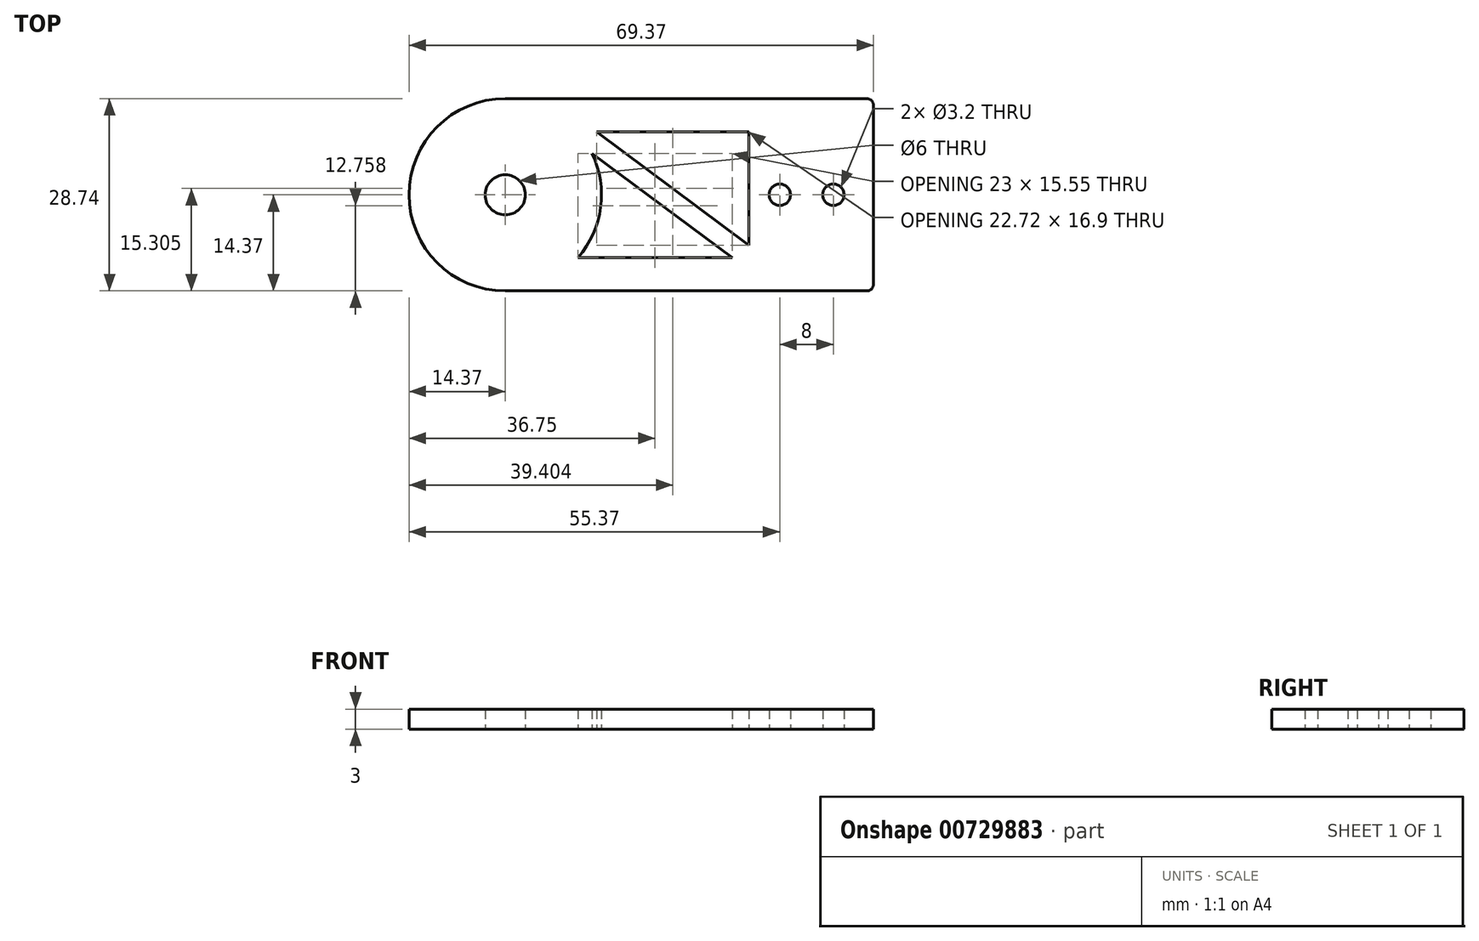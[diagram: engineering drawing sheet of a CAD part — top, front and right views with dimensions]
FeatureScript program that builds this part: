
annotation { "Feature Type Name" : "Feature", "Feature Type Description" : "" }
export const myFeature = defineFeature(function(context is Context, id is Id, definition is map)
    precondition{}
    {
        {
            var Q0;
            Q0=qCreatedBy(makeId("Top.planeOp"),FACE);
            var sketch = newSketch(context, id + "F0", { "sketchPlane" : qUnion([Q0])});
            skLineSegment(sketch, "E0.bottom", {"start": v(22.5, 0) * mm, "end": v(77.5, 0) * mm});
            skLineSegment(sketch, "E0.top", {"start": v(22.5, 28.74) * mm, "end": v(77.5, 28.74) * mm});
            skLineSegment(sketch, "E0.right", {"start": v(77.5, 0) * mm, "end": v(77.5, 28.74) * mm});
            skLineSegment(sketch, "E1", {"start": v(12.5, 14.37) * mm, "end": v(77.5, 14.37) * mm, "construction": true});
            skCircle(sketch, "E2", {"center": v(22.5, 14.37) * mm, "radius": 3 * mm});
            skArc(sketch, "E3", {"start": v(22.5, 28.74) * mm, "mid": v(8.13, 14.37) * mm, "end": v(22.5, 0) * mm});
            skPoint(sketch, "E4.orphan", {"position": v(25, 28.74) * mm});
            skPoint(sketch, "E5.orphan", {"position": v(0, 0) * mm});
            skCircle(sketch, "E6", {"center": v(71.5, 14.37) * mm, "radius": 1.6 * mm});
            skCircle(sketch, "E7", {"center": v(63.5, 14.37) * mm, "radius": 1.6 * mm});
            skLineSegment(sketch, "E8.bottom", {"start": v(56.38, 4.98) * mm, "end": v(33.38, 4.98) * mm});
            skLineSegment(sketch, "E8.top", {"start": v(58.9, 23.76) * mm, "end": v(36.17, 23.76) * mm});
            skLineSegment(sketch, "E8.left", {"start": v(58.9, 6.85) * mm, "end": v(58.9, 23.76) * mm});
            skLineSegment(sketch, "E8.right", {"start": v(33.66, 4.98) * mm, "end": v(33.66, 23.76) * mm, "construction": true});
            skPoint(sketch, "E8.middle", {"position": v(46.28, 14.37) * mm});
            skLineSegment(sketch, "E9", {"start": v(33.66, 23.76) * mm, "end": v(58.9, 4.98) * mm, "construction": true});
            skLineSegment(sketch, "E10.MirrorCS", {"start": v(36.17, 23.76) * mm, "end": v(58.9, 6.85) * mm});
            skLineSegment(sketch, "E11.trimOffspring", {"start": v(35.48, 20.53) * mm, "end": v(56.38, 4.98) * mm});
            skPoint(sketch, "E12.0.start.orphan", {"position": v(32.77, 22.55) * mm});
            skArc(sketch, "E13.trimOffspring", {"start": v(35.48, 20.53) * mm, "mid": v(36.74, 12.45) * mm, "end": v(33.38, 4.98) * mm});
            skPoint(sketch, "E14.orphan", {"position": v(34.56, 24.96) * mm});
            skPoint(sketch, "E15.orphan", {"position": v(59.79, 6.19) * mm});
            skPoint(sketch, "E16.orphan", {"position": v(58, 3.78) * mm});
            skSolve(sketch);
        }
        {
            var Q0;
            Q0=makeQuery(id+"F0.imprint","IMPRINT",FACE,{"disambiguationData":[TD([[makeQuery(id+"F0.imprint","IMPRINT",EDGE,{"derivedFrom":sQuery(id+"F0.wireOp",EDGE,"E0.bottom")}),1.0]])]});
            extrude(context, id + "F1", {"entities" : qUnion([Q0]), "depth" : 3 * mm, "offsetDistance" : 25 * mm});
        }
        {
            var Q0;
            Q0=makeQuery(id+"F1.opExtrude","SWEPT_EDGE",EDGE,{"disambiguationData":[OSD([sQuery(id+"F0.wireOp",EDGE,"E0.bottom"),sQuery(id+"F0.wireOp",EDGE,"E0.right")])]});
            var Q1;
            Q1=makeQuery(id+"F1.opExtrude","SWEPT_EDGE",EDGE,{"disambiguationData":[OSD([sQuery(id+"F0.wireOp",EDGE,"E0.top"),sQuery(id+"F0.wireOp",EDGE,"E0.right")])]});
            fillet(context, id + "F2", {"entities" : qUnion([Q0, Q1]), "radius" : 1 * mm, "tangentPropagation" : true, "allowEdgeOverflow" : false});
        }
    });
